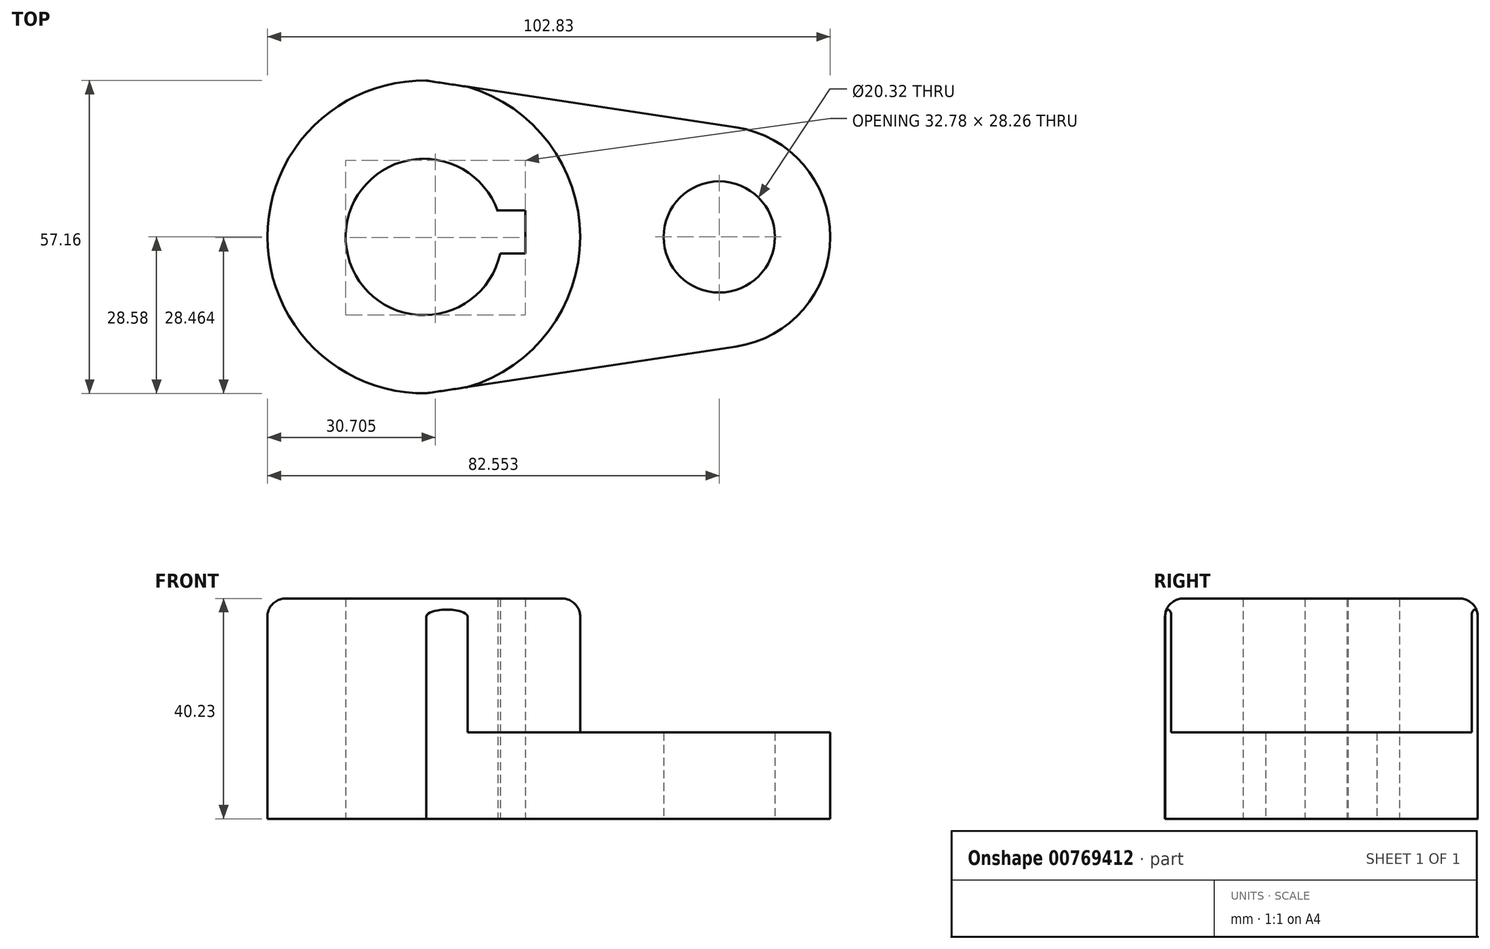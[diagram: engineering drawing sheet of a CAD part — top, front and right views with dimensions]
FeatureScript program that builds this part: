
annotation { "Feature Type Name" : "Feature", "Feature Type Description" : "" }
export const myFeature = defineFeature(function(context is Context, id is Id, definition is map)
    precondition{}
    {
        {
            var Q0;
            Q0=qCreatedBy(makeId("Top.planeOp"),FACE);
            var sketch = newSketch(context, id + "F0", { "sketchPlane" : qUnion([Q0])});
            skCircle(sketch, "E0", {"center": v(-45.08, 0) * mm, "radius": 28.58 * mm});
            skArc(sketch, "E1", {"start": v(-31.58, 4.67) * mm, "mid": v(-59.34, -0.85) * mm, "end": v(-31.12, -3.03) * mm});
            skLineSegment(sketch, "E2.top", {"start": v(-31.58, 4.88) * mm, "end": v(-26.57, 4.88) * mm});
            skLineSegment(sketch, "E2.left", {"start": v(-31.58, 4.67) * mm, "end": v(-31.58, 4.88) * mm});
            skLineSegment(sketch, "E2.right", {"start": v(-26.57, 4.67) * mm, "end": v(-26.57, 4.88) * mm});
            skLineSegment(sketch, "E3.bottom", {"start": v(-26.57, 4.67) * mm, "end": v(-26.57, 4.67) * mm});
            skLineSegment(sketch, "E3.top", {"start": v(-26.57, -3.2) * mm, "end": v(-26.57, -3.2) * mm});
            skLineSegment(sketch, "E3.left", {"start": v(-26.57, 0.73) * mm, "end": v(-26.57, -3.03) * mm});
            skLineSegment(sketch, "E3.right", {"start": v(-26.57, 4.67) * mm, "end": v(-26.57, -3.03) * mm});
            skLineSegment(sketch, "E4.top", {"start": v(-26.57, -3.03) * mm, "end": v(-31.12, -3.03) * mm});
            skPoint(sketch, "E5.oppositeSnap0", {"position": v(-26.57, 0.73) * mm});
            skLineSegment(sketch, "E5.left", {"start": v(-26.57, 0.73) * mm, "end": v(-26.57, 0.73) * mm});
            skLineSegment(sketch, "E5.right", {"start": v(-30.81, 0.73) * mm, "end": v(-30.81, 0.73) * mm});
            skPoint(sketch, "E4.left.end.orphan", {"position": v(-26.24, -3.03) * mm});
            skCircle(sketch, "E6", {"center": v(8.9, 0) * mm, "radius": 10.16 * mm});
            skArc(sketch, "E7", {"start": v(11.91, -20.05) * mm, "mid": v(29.17, 0) * mm, "end": v(11.91, 20.05) * mm});
            skLineSegment(sketch, "E8", {"start": v(-44.64, -28.57) * mm, "end": v(11.91, -20.05) * mm});
            skLineSegment(sketch, "E9", {"start": v(11.91, 20.05) * mm, "end": v(-44.64, 28.57) * mm});
            skSolve(sketch);
        }
        {
            var Q0;
            Q0=makeQuery(id+"F0.imprint","IMPRINT",FACE,{"disambiguationData":[TD([[makeQuery(id+"F0.imprint","IMPRINT",EDGE,{"derivedFrom":sQuery(id+"F0.wireOp",EDGE,"E1")}),-1.0]])]});
            extrude(context, id + "F1", {"entities" : qUnion([Q0]), "depth" : 40.23 * mm, "offsetDistance" : 25.4 * mm});
        }
        {
            var Q0;
            Q0=makeQuery(id+"F0.imprint","IMPRINT",FACE,{"disambiguationData":[TD([[makeQuery(id+"F0.imprint","IMPRINT",EDGE,{"derivedFrom":sQuery(id+"F0.wireOp",EDGE,"E6")}),-1.0]])]});
            extrude(context, id + "F2", {"entities" : qUnion([Q0]), "operationType" : NewBodyOperationType.ADD, "depth" : 15.77 * mm, "offsetDistance" : 25.4 * mm});
        }
        {
            var Q0;
            {var subQ0=sQuery(id+"F0.wireOp",EDGE,"E0");Q0=makeQuery(id+"F1.opExtrude","CAP_EDGE",EDGE,{"disambiguationData":[OSD([subQ0]),TDD([makeQuery(id+"F0.imprint","IMPRINT",EDGE,{"disambiguationData":[TD([[makeQuery(id+"F0.imprint","INTERSECT",VERTEX,{"disambiguationData":[OD(1.0)],"derivedFrom":[subQ0,sQuery(id+"F0.wireOp",EDGE,"E9")]}),1.0]])],"derivedFrom":subQ0})])],"isStart":false});}
            fillet(context, id + "F3", {"entities" : qUnion([Q0]), "radius" : 3.3 * mm, "tangentPropagation" : true, "allowEdgeOverflow" : false});
        }
    });
